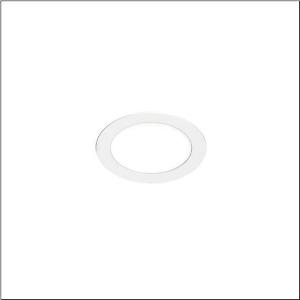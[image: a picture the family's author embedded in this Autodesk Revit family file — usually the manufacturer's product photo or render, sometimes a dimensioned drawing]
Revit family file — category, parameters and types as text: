
# Revit family: lunis_41_flat_51dr107dgba
name_source: partatom
category: Lighting Fixtures
units: mm (PartAtom-declared; Revit-internal decimal feet)

## family parameters
Cut with Voids When Loaded = No
Host = Face
Light Source = No
Part Type = Normal
Room Calculation Point = No
Round Connector Dimension = Use Diameter
Shared = No

## types (1)
- --- (1 x LED, 1360 lm, 15 W, 4000K)
    Apparent Load = 15 VA
    CIE Flux Codes = 49 80 96 100 100
    Color Rendering = 80
    Color Temperature = 4000K
    Default Elevation = 1800 mm
    Description = Lunis 41,  flat, downlight, light emission: direct distribution, LED rated luminous flux: 1.250lm, light colour: 830/840, control gear: ECG, mains connection: 230V, AC, 50/60Hz, housing, round, of aluminium, coated, traffic white (RAL 9016), diameter: 170mm, protection rating (complete): IP20, protection rating (on room side): IP44, insulation class (complete): insulation class II (safety insulation), certification: CE, permissible ambient temperature for indoor applications: -20..+40°C, packaging unit: 1 piece
    Height = 0 mm  [stored 0 ft]
    Lamp = 1 x LED
    Lamp Light Flux = 1360 lm
    Lamp Power = 15 W
    Lamp count = 1
    Length = 170 mm  [stored 0.557743 ft]
    Luminous efficacy = 91 lm/W
    Manufacturer = Siteco
    ModVariant = No
    Model = 51DR107DGBA
    Mounting Place = Ceiling
    Mounting Type = Recessed
    Number of Poles = 1
    OnlyDefault = Yes
    Power Factor = 1
    Product Name = Lunis 41 flat
    Product group = downlight
    ProductGroupID = 400
    Protection Class = Protection class II
    Protection Degree = IP 20
    RLX_Detail_Level = 1
    RLX_Emergency_Light_Flux = 0 lm
    RLX_Emergency_Type = 0
    RLX_Emergency_Type_DB = No
    RlxData = <blob elided: 24193 chars, md5=d310b7ca>
    Socket = socket
    Standby Power = 0 W
    System Light Flux = 1360 lm
    System Power = 15 W
    Type Comments = factory setting: colour temperature 4000K
    Type Image = l_1007045.jpg
    URL = http://relux.com
    VarID = @adj_130683
    Voltage = 0 V
    Weight = 0.00 kg
    Width = 0 mm  [stored 0 ft]

note: [stored X ft] marks values corroborated as IEEE doubles in the binary element streams (Revit-internal decimal feet)

## geometry (parser evidence)
native form markers: Blend x4, Sweep x11
no freeform markers — native parametric forms only
